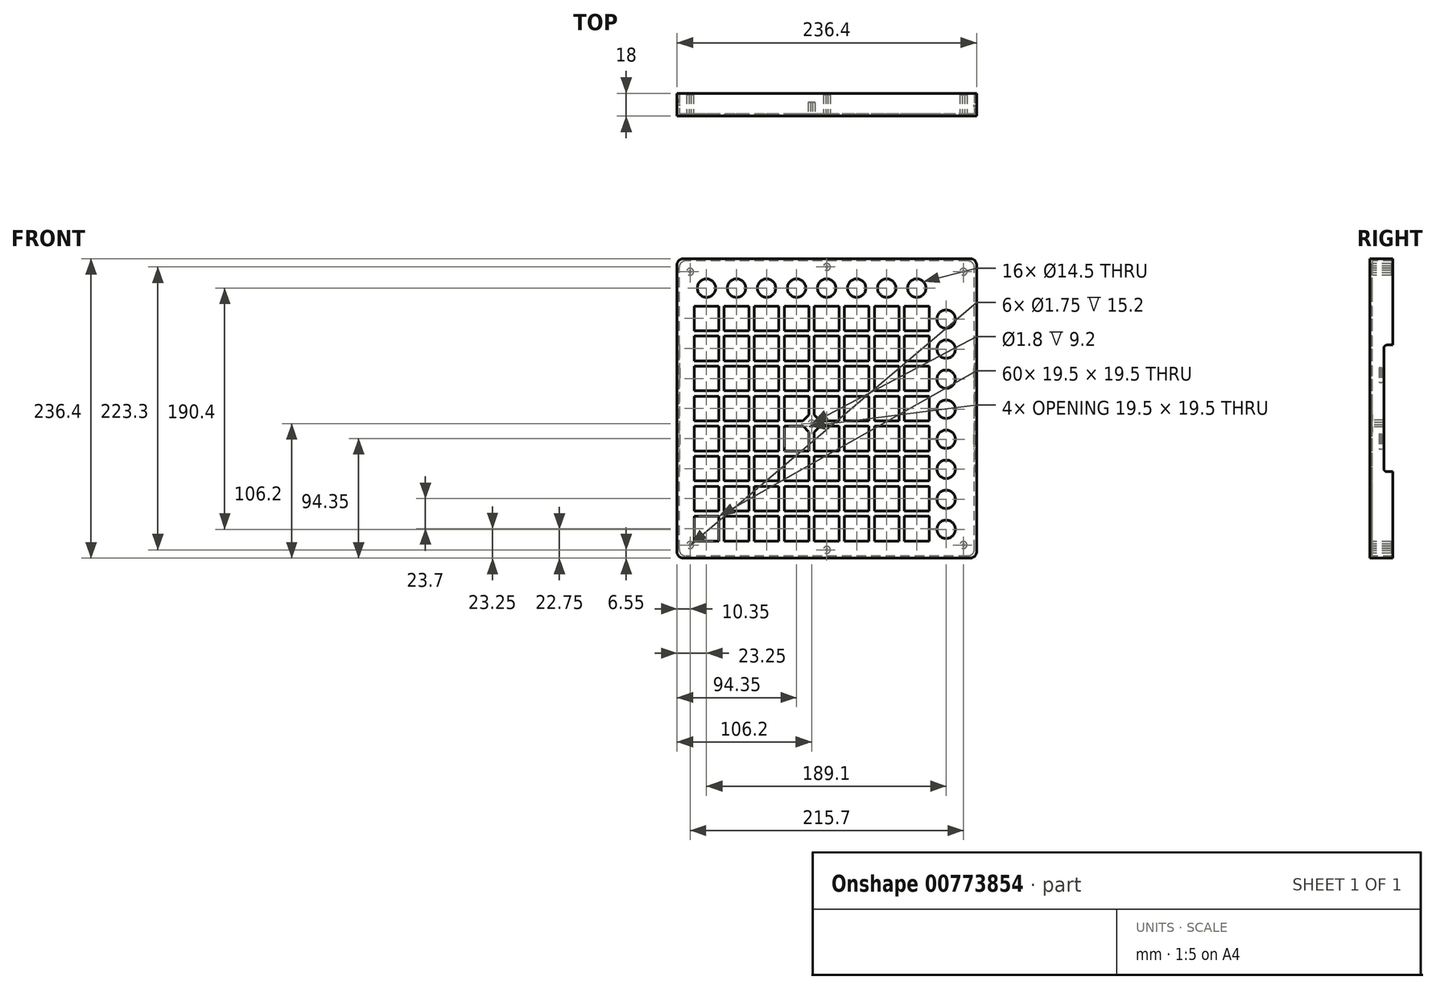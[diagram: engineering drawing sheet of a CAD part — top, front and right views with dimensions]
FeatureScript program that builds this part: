
annotation { "Feature Type Name" : "Feature", "Feature Type Description" : "" }
export const myFeature = defineFeature(function(context is Context, id is Id, definition is map)
    precondition{}
    {
        {
            var Q0;
            Q0=qCreatedBy(makeId("Front.planeOp"),FACE);
            var sketch = newSketch(context, id + "F0", { "sketchPlane" : qUnion([Q0]), "disableImprinting" : false});
            skLineSegment(sketch, "E0.bottom", {"start": v(113.2, -118.2) * mm, "end": v(-113.2, -118.2) * mm});
            skLineSegment(sketch, "E0.top", {"start": v(113.2, 118.2) * mm, "end": v(-113.2, 118.2) * mm});
            skLineSegment(sketch, "E0.left", {"start": v(118.2, -113.2) * mm, "end": v(118.2, 113.2) * mm});
            skLineSegment(sketch, "E0.right", {"start": v(-118.2, -113.2) * mm, "end": v(-118.2, 113.2) * mm});
            skPoint(sketch, "E0.middle", {"position": v(0, 0) * mm});
            skCircle(sketch, "E1", {"center": v(94.15, 70.45) * mm, "radius": 7.25 * mm});
            skCircle(sketch, "E2", {"center": v(94.15, 46.75) * mm, "radius": 7.25 * mm});
            skCircle(sketch, "E3", {"center": v(94.15, 23.05) * mm, "radius": 7.25 * mm});
            skCircle(sketch, "E4", {"center": v(94.15, -0.65) * mm, "radius": 7.25 * mm});
            skCircle(sketch, "E5", {"center": v(94.15, -24.35) * mm, "radius": 7.25 * mm});
            skCircle(sketch, "E6", {"center": v(94.15, -48.05) * mm, "radius": 7.25 * mm});
            skCircle(sketch, "E7", {"center": v(94.15, -71.75) * mm, "radius": 7.25 * mm});
            skCircle(sketch, "E8", {"center": v(94.15, -95.45) * mm, "radius": 7.25 * mm});
            skCircle(sketch, "E9", {"center": v(70.95, 94.95) * mm, "radius": 7.25 * mm});
            skCircle(sketch, "E10", {"center": v(23.55, 94.95) * mm, "radius": 7.25 * mm});
            skCircle(sketch, "E11", {"center": v(47.25, 94.95) * mm, "radius": 7.25 * mm});
            skCircle(sketch, "E12", {"center": v(-0.15, 94.95) * mm, "radius": 7.25 * mm});
            skCircle(sketch, "E13", {"center": v(-23.85, 94.95) * mm, "radius": 7.25 * mm});
            skCircle(sketch, "E14", {"center": v(-47.55, 94.95) * mm, "radius": 7.25 * mm});
            skCircle(sketch, "E15", {"center": v(-71.25, 94.95) * mm, "radius": 7.25 * mm});
            skCircle(sketch, "E16", {"center": v(-94.95, 94.95) * mm, "radius": 7.25 * mm});
            skLineSegment(sketch, "E17.bottom", {"start": v(80.7, 61.2) * mm, "end": v(61.2, 61.2) * mm});
            skLineSegment(sketch, "E17.top", {"start": v(80.7, 80.7) * mm, "end": v(61.2, 80.7) * mm});
            skLineSegment(sketch, "E17.left", {"start": v(80.7, 61.2) * mm, "end": v(80.7, 80.7) * mm});
            skLineSegment(sketch, "E17.right", {"start": v(61.2, 61.2) * mm, "end": v(61.2, 80.7) * mm});
            skPoint(sketch, "E17.middle", {"position": v(70.95, 70.95) * mm});
            skLineSegment(sketch, "E18.bottom", {"start": v(80.7, 37.5) * mm, "end": v(61.2, 37.5) * mm});
            skLineSegment(sketch, "E18.top", {"start": v(80.7, 57) * mm, "end": v(61.2, 57) * mm});
            skLineSegment(sketch, "E18.left", {"start": v(80.7, 37.5) * mm, "end": v(80.7, 57) * mm});
            skLineSegment(sketch, "E18.right", {"start": v(61.2, 37.5) * mm, "end": v(61.2, 57) * mm});
            skLineSegment(sketch, "E19.bottom", {"start": v(80.7, 13.8) * mm, "end": v(61.2, 13.8) * mm});
            skLineSegment(sketch, "E19.top", {"start": v(80.7, 33.3) * mm, "end": v(61.2, 33.3) * mm});
            skLineSegment(sketch, "E19.left", {"start": v(80.7, 13.8) * mm, "end": v(80.7, 33.3) * mm});
            skLineSegment(sketch, "E19.right", {"start": v(61.2, 13.8) * mm, "end": v(61.2, 33.3) * mm});
            skLineSegment(sketch, "E20.bottom", {"start": v(80.7, -9.9) * mm, "end": v(61.2, -9.9) * mm});
            skLineSegment(sketch, "E20.top", {"start": v(80.7, 9.6) * mm, "end": v(61.2, 9.6) * mm});
            skLineSegment(sketch, "E20.left", {"start": v(80.7, -9.9) * mm, "end": v(80.7, 9.6) * mm});
            skLineSegment(sketch, "E20.right", {"start": v(61.2, -9.9) * mm, "end": v(61.2, 9.6) * mm});
            skLineSegment(sketch, "E21.bottom", {"start": v(80.7, -33.6) * mm, "end": v(61.2, -33.6) * mm});
            skLineSegment(sketch, "E21.top", {"start": v(80.7, -14.1) * mm, "end": v(61.2, -14.1) * mm});
            skLineSegment(sketch, "E21.left", {"start": v(80.7, -33.6) * mm, "end": v(80.7, -14.1) * mm});
            skLineSegment(sketch, "E21.right", {"start": v(61.2, -33.6) * mm, "end": v(61.2, -14.1) * mm});
            skLineSegment(sketch, "E22.bottom", {"start": v(80.7, -57.3) * mm, "end": v(61.2, -57.3) * mm});
            skLineSegment(sketch, "E22.top", {"start": v(80.7, -37.8) * mm, "end": v(61.2, -37.8) * mm});
            skLineSegment(sketch, "E22.left", {"start": v(80.7, -57.3) * mm, "end": v(80.7, -37.8) * mm});
            skLineSegment(sketch, "E22.right", {"start": v(61.2, -57.3) * mm, "end": v(61.2, -37.8) * mm});
            skLineSegment(sketch, "E23.bottom", {"start": v(80.7, -81) * mm, "end": v(61.2, -81) * mm});
            skLineSegment(sketch, "E23.top", {"start": v(80.7, -61.5) * mm, "end": v(61.2, -61.5) * mm});
            skLineSegment(sketch, "E23.left", {"start": v(80.7, -81) * mm, "end": v(80.7, -61.5) * mm});
            skLineSegment(sketch, "E23.right", {"start": v(61.2, -81) * mm, "end": v(61.2, -61.5) * mm});
            skLineSegment(sketch, "E24.bottom", {"start": v(80.7, -104.7) * mm, "end": v(61.2, -104.7) * mm});
            skLineSegment(sketch, "E24.top", {"start": v(80.7, -85.2) * mm, "end": v(61.2, -85.2) * mm});
            skLineSegment(sketch, "E24.left", {"start": v(80.7, -104.7) * mm, "end": v(80.7, -85.2) * mm});
            skLineSegment(sketch, "E24.right", {"start": v(61.2, -104.7) * mm, "end": v(61.2, -85.2) * mm});
            skLineSegment(sketch, "E25.bottom", {"start": v(57, 61.2) * mm, "end": v(37.5, 61.2) * mm});
            skLineSegment(sketch, "E25.top", {"start": v(57, 80.7) * mm, "end": v(37.5, 80.7) * mm});
            skLineSegment(sketch, "E25.left", {"start": v(57, 61.2) * mm, "end": v(57, 80.7) * mm});
            skLineSegment(sketch, "E25.right", {"start": v(37.5, 61.2) * mm, "end": v(37.5, 80.7) * mm});
            skLineSegment(sketch, "E26.bottom", {"start": v(57, 37.5) * mm, "end": v(37.5, 37.5) * mm});
            skLineSegment(sketch, "E26.top", {"start": v(57, 57) * mm, "end": v(37.5, 57) * mm});
            skLineSegment(sketch, "E26.left", {"start": v(57, 37.5) * mm, "end": v(57, 57) * mm});
            skLineSegment(sketch, "E26.right", {"start": v(37.5, 37.5) * mm, "end": v(37.5, 57) * mm});
            skLineSegment(sketch, "E27.bottom", {"start": v(57, 13.8) * mm, "end": v(37.5, 13.8) * mm});
            skLineSegment(sketch, "E27.top", {"start": v(57, 33.3) * mm, "end": v(37.5, 33.3) * mm});
            skLineSegment(sketch, "E27.left", {"start": v(57, 13.8) * mm, "end": v(57, 33.3) * mm});
            skLineSegment(sketch, "E27.right", {"start": v(37.5, 13.8) * mm, "end": v(37.5, 33.3) * mm});
            skLineSegment(sketch, "E28.bottom", {"start": v(57, -9.9) * mm, "end": v(37.5, -9.9) * mm});
            skLineSegment(sketch, "E28.top", {"start": v(57, 9.6) * mm, "end": v(37.5, 9.6) * mm});
            skLineSegment(sketch, "E28.left", {"start": v(57, -9.9) * mm, "end": v(57, 9.6) * mm});
            skLineSegment(sketch, "E28.right", {"start": v(37.5, -9.9) * mm, "end": v(37.5, 9.6) * mm});
            skLineSegment(sketch, "E29.bottom", {"start": v(57, -33.6) * mm, "end": v(37.5, -33.6) * mm});
            skLineSegment(sketch, "E29.top", {"start": v(57, -14.1) * mm, "end": v(37.5, -14.1) * mm});
            skLineSegment(sketch, "E29.left", {"start": v(57, -33.6) * mm, "end": v(57, -14.1) * mm});
            skLineSegment(sketch, "E29.right", {"start": v(37.5, -33.6) * mm, "end": v(37.5, -14.1) * mm});
            skLineSegment(sketch, "E30.bottom", {"start": v(57, -57.3) * mm, "end": v(37.5, -57.3) * mm});
            skLineSegment(sketch, "E30.top", {"start": v(57, -37.8) * mm, "end": v(37.5, -37.8) * mm});
            skLineSegment(sketch, "E30.left", {"start": v(57, -57.3) * mm, "end": v(57, -37.8) * mm});
            skLineSegment(sketch, "E30.right", {"start": v(37.5, -57.3) * mm, "end": v(37.5, -37.8) * mm});
            skLineSegment(sketch, "E31.bottom", {"start": v(57, -81) * mm, "end": v(37.5, -81) * mm});
            skLineSegment(sketch, "E31.top", {"start": v(57, -61.5) * mm, "end": v(37.5, -61.5) * mm});
            skLineSegment(sketch, "E31.left", {"start": v(57, -81) * mm, "end": v(57, -61.5) * mm});
            skLineSegment(sketch, "E31.right", {"start": v(37.5, -81) * mm, "end": v(37.5, -61.5) * mm});
            skLineSegment(sketch, "E32.bottom", {"start": v(57, -104.7) * mm, "end": v(37.5, -104.7) * mm});
            skLineSegment(sketch, "E32.top", {"start": v(57, -85.2) * mm, "end": v(37.5, -85.2) * mm});
            skLineSegment(sketch, "E32.left", {"start": v(57, -104.7) * mm, "end": v(57, -85.2) * mm});
            skLineSegment(sketch, "E33", {"start": v(37.5, -85.2) * mm, "end": v(37.5, -104.7) * mm});
            skLineSegment(sketch, "E34.bottom", {"start": v(33.3, 61.2) * mm, "end": v(13.8, 61.2) * mm});
            skLineSegment(sketch, "E34.top", {"start": v(33.3, 80.7) * mm, "end": v(13.8, 80.7) * mm});
            skLineSegment(sketch, "E34.left", {"start": v(33.3, 61.2) * mm, "end": v(33.3, 80.7) * mm});
            skLineSegment(sketch, "E34.right", {"start": v(13.8, 61.2) * mm, "end": v(13.8, 80.7) * mm});
            skLineSegment(sketch, "E35.bottom", {"start": v(33.3, 37.5) * mm, "end": v(13.8, 37.5) * mm});
            skLineSegment(sketch, "E35.top", {"start": v(33.3, 57) * mm, "end": v(13.8, 57) * mm});
            skLineSegment(sketch, "E35.left", {"start": v(33.3, 37.5) * mm, "end": v(33.3, 57) * mm});
            skLineSegment(sketch, "E35.right", {"start": v(13.8, 37.5) * mm, "end": v(13.8, 57) * mm});
            skLineSegment(sketch, "E36.bottom", {"start": v(33.3, 13.8) * mm, "end": v(13.8, 13.8) * mm});
            skLineSegment(sketch, "E36.top", {"start": v(33.3, 33.3) * mm, "end": v(13.8, 33.3) * mm});
            skLineSegment(sketch, "E36.left", {"start": v(33.3, 13.8) * mm, "end": v(33.3, 33.3) * mm});
            skLineSegment(sketch, "E36.right", {"start": v(13.8, 13.8) * mm, "end": v(13.8, 33.3) * mm});
            skLineSegment(sketch, "E37.bottom", {"start": v(33.3, -9.9) * mm, "end": v(13.8, -9.9) * mm});
            skLineSegment(sketch, "E37.top", {"start": v(33.3, 9.6) * mm, "end": v(13.8, 9.6) * mm});
            skLineSegment(sketch, "E37.left", {"start": v(33.3, -9.9) * mm, "end": v(33.3, 9.6) * mm});
            skLineSegment(sketch, "E37.right", {"start": v(13.8, -9.9) * mm, "end": v(13.8, 9.6) * mm});
            skLineSegment(sketch, "E38.bottom", {"start": v(33.3, -33.6) * mm, "end": v(13.8, -33.6) * mm});
            skLineSegment(sketch, "E38.top", {"start": v(33.3, -14.1) * mm, "end": v(13.8, -14.1) * mm});
            skLineSegment(sketch, "E38.left", {"start": v(33.3, -33.6) * mm, "end": v(33.3, -14.1) * mm});
            skLineSegment(sketch, "E38.right", {"start": v(13.8, -33.6) * mm, "end": v(13.8, -14.1) * mm});
            skLineSegment(sketch, "E39.bottom", {"start": v(33.3, -57.3) * mm, "end": v(13.8, -57.3) * mm});
            skLineSegment(sketch, "E39.top", {"start": v(33.3, -37.8) * mm, "end": v(13.8, -37.8) * mm});
            skLineSegment(sketch, "E39.left", {"start": v(33.3, -57.3) * mm, "end": v(33.3, -37.8) * mm});
            skLineSegment(sketch, "E39.right", {"start": v(13.8, -57.3) * mm, "end": v(13.8, -37.8) * mm});
            skLineSegment(sketch, "E40.bottom", {"start": v(33.3, -81) * mm, "end": v(13.8, -81) * mm});
            skLineSegment(sketch, "E40.top", {"start": v(33.3, -61.5) * mm, "end": v(13.8, -61.5) * mm});
            skLineSegment(sketch, "E40.left", {"start": v(33.3, -81) * mm, "end": v(33.3, -61.5) * mm});
            skLineSegment(sketch, "E40.right", {"start": v(13.8, -81) * mm, "end": v(13.8, -61.5) * mm});
            skLineSegment(sketch, "E41.bottom", {"start": v(33.3, -104.7) * mm, "end": v(13.8, -104.7) * mm});
            skLineSegment(sketch, "E41.top", {"start": v(33.3, -85.2) * mm, "end": v(13.8, -85.2) * mm});
            skLineSegment(sketch, "E41.left", {"start": v(33.3, -104.7) * mm, "end": v(33.3, -85.2) * mm});
            skLineSegment(sketch, "E42.bottom", {"start": v(9.6, 61.2) * mm, "end": v(-9.9, 61.2) * mm});
            skLineSegment(sketch, "E42.top", {"start": v(9.6, 80.7) * mm, "end": v(-9.9, 80.7) * mm});
            skLineSegment(sketch, "E42.left", {"start": v(9.6, 61.2) * mm, "end": v(9.6, 80.7) * mm});
            skLineSegment(sketch, "E42.right", {"start": v(-9.9, 61.2) * mm, "end": v(-9.9, 80.7) * mm});
            skLineSegment(sketch, "E43.bottom", {"start": v(9.6, 37.5) * mm, "end": v(-9.9, 37.5) * mm});
            skLineSegment(sketch, "E43.top", {"start": v(9.6, 57) * mm, "end": v(-9.9, 57) * mm});
            skLineSegment(sketch, "E43.left", {"start": v(9.6, 37.5) * mm, "end": v(9.6, 57) * mm});
            skLineSegment(sketch, "E43.right", {"start": v(-9.9, 37.5) * mm, "end": v(-9.9, 57) * mm});
            skLineSegment(sketch, "E44.bottom", {"start": v(9.6, 13.8) * mm, "end": v(-9.9, 13.8) * mm});
            skLineSegment(sketch, "E44.top", {"start": v(9.6, 33.3) * mm, "end": v(-9.9, 33.3) * mm});
            skLineSegment(sketch, "E44.left", {"start": v(9.6, 13.8) * mm, "end": v(9.6, 33.3) * mm});
            skLineSegment(sketch, "E44.right", {"start": v(-9.9, 13.8) * mm, "end": v(-9.9, 33.3) * mm});
            skLineSegment(sketch, "E45.bottom", {"start": v(9.6, -9.9) * mm, "end": v(-9.9, -9.9) * mm});
            skLineSegment(sketch, "E45.top", {"start": v(9.6, 9.6) * mm, "end": v(-9.9, 9.6) * mm});
            skLineSegment(sketch, "E45.left", {"start": v(9.6, -9.9) * mm, "end": v(9.6, 9.6) * mm});
            skLineSegment(sketch, "E45.right", {"start": v(-9.9, -9.9) * mm, "end": v(-9.9, 9.6) * mm});
            skLineSegment(sketch, "E46.bottom", {"start": v(9.6, -33.6) * mm, "end": v(-9.9, -33.6) * mm});
            skLineSegment(sketch, "E46.top", {"start": v(9.6, -14.1) * mm, "end": v(-9.9, -14.1) * mm});
            skLineSegment(sketch, "E46.left", {"start": v(9.6, -33.6) * mm, "end": v(9.6, -14.1) * mm});
            skLineSegment(sketch, "E46.right", {"start": v(-9.9, -33.6) * mm, "end": v(-9.9, -14.1) * mm});
            skLineSegment(sketch, "E47.bottom", {"start": v(9.6, -57.3) * mm, "end": v(-9.9, -57.3) * mm});
            skLineSegment(sketch, "E47.top", {"start": v(9.6, -37.8) * mm, "end": v(-9.9, -37.8) * mm});
            skLineSegment(sketch, "E47.left", {"start": v(9.6, -57.3) * mm, "end": v(9.6, -37.8) * mm});
            skLineSegment(sketch, "E47.right", {"start": v(-9.9, -57.3) * mm, "end": v(-9.9, -37.8) * mm});
            skLineSegment(sketch, "E48.bottom", {"start": v(9.6, -81) * mm, "end": v(-9.9, -81) * mm});
            skLineSegment(sketch, "E48.top", {"start": v(9.6, -61.5) * mm, "end": v(-9.9, -61.5) * mm});
            skLineSegment(sketch, "E48.left", {"start": v(9.6, -81) * mm, "end": v(9.6, -61.5) * mm});
            skLineSegment(sketch, "E48.right", {"start": v(-9.9, -81) * mm, "end": v(-9.9, -61.5) * mm});
            skLineSegment(sketch, "E49.bottom", {"start": v(9.6, -104.7) * mm, "end": v(-9.9, -104.7) * mm});
            skLineSegment(sketch, "E49.top", {"start": v(9.6, -85.2) * mm, "end": v(-9.9, -85.2) * mm});
            skLineSegment(sketch, "E49.left", {"start": v(9.6, -104.7) * mm, "end": v(9.6, -85.2) * mm});
            skLineSegment(sketch, "E50", {"start": v(13.8, -85.2) * mm, "end": v(13.8, -104.7) * mm});
            skLineSegment(sketch, "E51", {"start": v(-9.9, -85.2) * mm, "end": v(-9.9, -104.7) * mm});
            skLineSegment(sketch, "E52.bottom", {"start": v(-14.1, 61.2) * mm, "end": v(-33.6, 61.2) * mm});
            skLineSegment(sketch, "E52.top", {"start": v(-14.1, 80.7) * mm, "end": v(-33.6, 80.7) * mm});
            skLineSegment(sketch, "E52.left", {"start": v(-14.1, 61.2) * mm, "end": v(-14.1, 80.7) * mm});
            skLineSegment(sketch, "E52.right", {"start": v(-33.6, 61.2) * mm, "end": v(-33.6, 80.7) * mm});
            skLineSegment(sketch, "E53.bottom", {"start": v(-14.1, 37.5) * mm, "end": v(-33.6, 37.5) * mm});
            skLineSegment(sketch, "E53.top", {"start": v(-14.1, 57) * mm, "end": v(-33.6, 57) * mm});
            skLineSegment(sketch, "E53.left", {"start": v(-14.1, 37.5) * mm, "end": v(-14.1, 57) * mm});
            skLineSegment(sketch, "E53.right", {"start": v(-33.6, 37.5) * mm, "end": v(-33.6, 57) * mm});
            skLineSegment(sketch, "E54.bottom", {"start": v(-14.1, 13.8) * mm, "end": v(-33.6, 13.8) * mm});
            skLineSegment(sketch, "E54.top", {"start": v(-14.1, 33.3) * mm, "end": v(-33.6, 33.3) * mm});
            skLineSegment(sketch, "E54.left", {"start": v(-14.1, 13.8) * mm, "end": v(-14.1, 33.3) * mm});
            skLineSegment(sketch, "E54.right", {"start": v(-33.6, 13.8) * mm, "end": v(-33.6, 33.3) * mm});
            skLineSegment(sketch, "E55.bottom", {"start": v(-14.1, -9.9) * mm, "end": v(-33.6, -9.9) * mm});
            skLineSegment(sketch, "E55.top", {"start": v(-14.1, 9.6) * mm, "end": v(-33.6, 9.6) * mm});
            skLineSegment(sketch, "E55.left", {"start": v(-14.1, -9.9) * mm, "end": v(-14.1, 9.6) * mm});
            skLineSegment(sketch, "E55.right", {"start": v(-33.6, -9.9) * mm, "end": v(-33.6, 9.6) * mm});
            skLineSegment(sketch, "E56.bottom", {"start": v(-14.1, -33.6) * mm, "end": v(-33.6, -33.6) * mm});
            skLineSegment(sketch, "E56.top", {"start": v(-14.1, -14.1) * mm, "end": v(-33.6, -14.1) * mm});
            skLineSegment(sketch, "E56.left", {"start": v(-14.1, -33.6) * mm, "end": v(-14.1, -14.1) * mm});
            skLineSegment(sketch, "E56.right", {"start": v(-33.6, -33.6) * mm, "end": v(-33.6, -14.1) * mm});
            skLineSegment(sketch, "E57.bottom", {"start": v(-14.1, -57.3) * mm, "end": v(-33.6, -57.3) * mm});
            skLineSegment(sketch, "E57.top", {"start": v(-14.1, -37.8) * mm, "end": v(-33.6, -37.8) * mm});
            skLineSegment(sketch, "E57.left", {"start": v(-14.1, -57.3) * mm, "end": v(-14.1, -37.8) * mm});
            skLineSegment(sketch, "E57.right", {"start": v(-33.6, -57.3) * mm, "end": v(-33.6, -37.8) * mm});
            skLineSegment(sketch, "E58.bottom", {"start": v(-14.1, -81) * mm, "end": v(-33.6, -81) * mm});
            skLineSegment(sketch, "E58.top", {"start": v(-14.1, -61.5) * mm, "end": v(-33.6, -61.5) * mm});
            skLineSegment(sketch, "E58.left", {"start": v(-14.1, -81) * mm, "end": v(-14.1, -61.5) * mm});
            skLineSegment(sketch, "E58.right", {"start": v(-33.6, -81) * mm, "end": v(-33.6, -61.5) * mm});
            skLineSegment(sketch, "E59.bottom", {"start": v(-14.1, -104.7) * mm, "end": v(-33.6, -104.7) * mm});
            skLineSegment(sketch, "E59.top", {"start": v(-14.1, -85.2) * mm, "end": v(-33.6, -85.2) * mm});
            skLineSegment(sketch, "E59.left", {"start": v(-14.1, -104.7) * mm, "end": v(-14.1, -85.2) * mm});
            skLineSegment(sketch, "E60", {"start": v(-33.6, -85.2) * mm, "end": v(-33.6, -104.7) * mm});
            skLineSegment(sketch, "E61.bottom", {"start": v(-37.8, 61.2) * mm, "end": v(-57.3, 61.2) * mm});
            skLineSegment(sketch, "E61.top", {"start": v(-37.8, 80.7) * mm, "end": v(-57.3, 80.7) * mm});
            skLineSegment(sketch, "E61.left", {"start": v(-37.8, 61.2) * mm, "end": v(-37.8, 80.7) * mm});
            skLineSegment(sketch, "E61.right", {"start": v(-57.3, 61.2) * mm, "end": v(-57.3, 80.7) * mm});
            skLineSegment(sketch, "E62.bottom", {"start": v(-37.8, 37.5) * mm, "end": v(-57.3, 37.5) * mm});
            skLineSegment(sketch, "E62.top", {"start": v(-37.8, 57) * mm, "end": v(-57.3, 57) * mm});
            skLineSegment(sketch, "E62.left", {"start": v(-37.8, 37.5) * mm, "end": v(-37.8, 57) * mm});
            skLineSegment(sketch, "E62.right", {"start": v(-57.3, 37.5) * mm, "end": v(-57.3, 57) * mm});
            skLineSegment(sketch, "E63.bottom", {"start": v(-37.8, 13.8) * mm, "end": v(-57.3, 13.8) * mm});
            skLineSegment(sketch, "E63.top", {"start": v(-37.8, 33.3) * mm, "end": v(-57.3, 33.3) * mm});
            skLineSegment(sketch, "E63.left", {"start": v(-37.8, 13.8) * mm, "end": v(-37.8, 33.3) * mm});
            skLineSegment(sketch, "E63.right", {"start": v(-57.3, 13.8) * mm, "end": v(-57.3, 33.3) * mm});
            skLineSegment(sketch, "E64.bottom", {"start": v(-37.8, -9.9) * mm, "end": v(-57.3, -9.9) * mm});
            skLineSegment(sketch, "E64.top", {"start": v(-37.8, 9.6) * mm, "end": v(-57.3, 9.6) * mm});
            skLineSegment(sketch, "E64.left", {"start": v(-37.8, -9.9) * mm, "end": v(-37.8, 9.6) * mm});
            skLineSegment(sketch, "E64.right", {"start": v(-57.3, -9.9) * mm, "end": v(-57.3, 9.6) * mm});
            skLineSegment(sketch, "E65.bottom", {"start": v(-37.8, -33.6) * mm, "end": v(-57.3, -33.6) * mm});
            skLineSegment(sketch, "E65.top", {"start": v(-37.8, -14.1) * mm, "end": v(-57.3, -14.1) * mm});
            skLineSegment(sketch, "E65.left", {"start": v(-37.8, -33.6) * mm, "end": v(-37.8, -14.1) * mm});
            skLineSegment(sketch, "E65.right", {"start": v(-57.3, -33.6) * mm, "end": v(-57.3, -14.1) * mm});
            skLineSegment(sketch, "E66.bottom", {"start": v(-37.8, -57.3) * mm, "end": v(-57.3, -57.3) * mm});
            skLineSegment(sketch, "E66.top", {"start": v(-37.8, -37.8) * mm, "end": v(-57.3, -37.8) * mm});
            skLineSegment(sketch, "E66.left", {"start": v(-37.8, -57.3) * mm, "end": v(-37.8, -37.8) * mm});
            skLineSegment(sketch, "E66.right", {"start": v(-57.3, -57.3) * mm, "end": v(-57.3, -37.8) * mm});
            skLineSegment(sketch, "E67.bottom", {"start": v(-37.8, -81) * mm, "end": v(-57.3, -81) * mm});
            skLineSegment(sketch, "E67.top", {"start": v(-37.8, -61.5) * mm, "end": v(-57.3, -61.5) * mm});
            skLineSegment(sketch, "E67.left", {"start": v(-37.8, -81) * mm, "end": v(-37.8, -61.5) * mm});
            skLineSegment(sketch, "E67.right", {"start": v(-57.3, -81) * mm, "end": v(-57.3, -61.5) * mm});
            skLineSegment(sketch, "E68.bottom", {"start": v(-37.8, -104.7) * mm, "end": v(-57.3, -104.7) * mm});
            skLineSegment(sketch, "E68.top", {"start": v(-37.8, -85.2) * mm, "end": v(-57.3, -85.2) * mm});
            skLineSegment(sketch, "E68.left", {"start": v(-37.8, -104.7) * mm, "end": v(-37.8, -85.2) * mm});
            skLineSegment(sketch, "E69.bottom", {"start": v(-61.5, 61.2) * mm, "end": v(-81, 61.2) * mm});
            skLineSegment(sketch, "E69.top", {"start": v(-61.5, 80.7) * mm, "end": v(-81, 80.7) * mm});
            skLineSegment(sketch, "E69.left", {"start": v(-61.5, 61.2) * mm, "end": v(-61.5, 80.7) * mm});
            skLineSegment(sketch, "E69.right", {"start": v(-81, 61.2) * mm, "end": v(-81, 80.7) * mm});
            skLineSegment(sketch, "E70.bottom", {"start": v(-61.5, 37.5) * mm, "end": v(-81, 37.5) * mm});
            skLineSegment(sketch, "E70.top", {"start": v(-61.5, 57) * mm, "end": v(-81, 57) * mm});
            skLineSegment(sketch, "E70.left", {"start": v(-61.5, 37.5) * mm, "end": v(-61.5, 57) * mm});
            skLineSegment(sketch, "E70.right", {"start": v(-81, 37.5) * mm, "end": v(-81, 57) * mm});
            skLineSegment(sketch, "E71.bottom", {"start": v(-61.5, 13.8) * mm, "end": v(-81, 13.8) * mm});
            skLineSegment(sketch, "E71.top", {"start": v(-61.5, 33.3) * mm, "end": v(-81, 33.3) * mm});
            skLineSegment(sketch, "E71.left", {"start": v(-61.5, 13.8) * mm, "end": v(-61.5, 33.3) * mm});
            skLineSegment(sketch, "E71.right", {"start": v(-81, 13.8) * mm, "end": v(-81, 33.3) * mm});
            skLineSegment(sketch, "E72.bottom", {"start": v(-61.5, -9.9) * mm, "end": v(-81, -9.9) * mm});
            skLineSegment(sketch, "E72.top", {"start": v(-61.5, 9.6) * mm, "end": v(-81, 9.6) * mm});
            skLineSegment(sketch, "E72.left", {"start": v(-61.5, -9.9) * mm, "end": v(-61.5, 9.6) * mm});
            skLineSegment(sketch, "E72.right", {"start": v(-81, -9.9) * mm, "end": v(-81, 9.6) * mm});
            skLineSegment(sketch, "E73.bottom", {"start": v(-61.5, -33.6) * mm, "end": v(-81, -33.6) * mm});
            skLineSegment(sketch, "E73.top", {"start": v(-61.5, -14.1) * mm, "end": v(-81, -14.1) * mm});
            skLineSegment(sketch, "E73.left", {"start": v(-61.5, -33.6) * mm, "end": v(-61.5, -14.1) * mm});
            skLineSegment(sketch, "E73.right", {"start": v(-81, -33.6) * mm, "end": v(-81, -14.1) * mm});
            skLineSegment(sketch, "E74.bottom", {"start": v(-61.5, -57.3) * mm, "end": v(-81, -57.3) * mm});
            skLineSegment(sketch, "E74.top", {"start": v(-61.5, -37.8) * mm, "end": v(-81, -37.8) * mm});
            skLineSegment(sketch, "E74.left", {"start": v(-61.5, -57.3) * mm, "end": v(-61.5, -37.8) * mm});
            skLineSegment(sketch, "E74.right", {"start": v(-81, -57.3) * mm, "end": v(-81, -37.8) * mm});
            skLineSegment(sketch, "E75.bottom", {"start": v(-61.5, -81) * mm, "end": v(-81, -81) * mm});
            skLineSegment(sketch, "E75.top", {"start": v(-61.5, -61.5) * mm, "end": v(-81, -61.5) * mm});
            skLineSegment(sketch, "E75.left", {"start": v(-61.5, -81) * mm, "end": v(-61.5, -61.5) * mm});
            skLineSegment(sketch, "E75.right", {"start": v(-81, -81) * mm, "end": v(-81, -61.5) * mm});
            skLineSegment(sketch, "E76.bottom", {"start": v(-61.5, -104.7) * mm, "end": v(-81, -104.7) * mm});
            skLineSegment(sketch, "E76.top", {"start": v(-61.5, -85.2) * mm, "end": v(-81, -85.2) * mm});
            skLineSegment(sketch, "E76.left", {"start": v(-61.5, -104.7) * mm, "end": v(-61.5, -85.2) * mm});
            skLineSegment(sketch, "E77.bottom", {"start": v(-85.2, 61.2) * mm, "end": v(-104.7, 61.2) * mm});
            skLineSegment(sketch, "E77.top", {"start": v(-85.2, 80.7) * mm, "end": v(-104.7, 80.7) * mm});
            skLineSegment(sketch, "E77.left", {"start": v(-85.2, 61.2) * mm, "end": v(-85.2, 80.7) * mm});
            skLineSegment(sketch, "E77.right", {"start": v(-104.7, 61.2) * mm, "end": v(-104.7, 80.7) * mm});
            skLineSegment(sketch, "E78.bottom", {"start": v(-85.2, 37.5) * mm, "end": v(-104.7, 37.5) * mm});
            skLineSegment(sketch, "E78.top", {"start": v(-85.2, 57) * mm, "end": v(-104.7, 57) * mm});
            skLineSegment(sketch, "E78.left", {"start": v(-85.2, 37.5) * mm, "end": v(-85.2, 57) * mm});
            skLineSegment(sketch, "E78.right", {"start": v(-104.7, 37.5) * mm, "end": v(-104.7, 57) * mm});
            skLineSegment(sketch, "E79.bottom", {"start": v(-85.2, 13.8) * mm, "end": v(-104.7, 13.8) * mm});
            skLineSegment(sketch, "E79.top", {"start": v(-85.2, 33.3) * mm, "end": v(-104.7, 33.3) * mm});
            skLineSegment(sketch, "E79.left", {"start": v(-85.2, 13.8) * mm, "end": v(-85.2, 33.3) * mm});
            skLineSegment(sketch, "E79.right", {"start": v(-104.7, 13.8) * mm, "end": v(-104.7, 33.3) * mm});
            skLineSegment(sketch, "E80.bottom", {"start": v(-85.2, -9.9) * mm, "end": v(-104.7, -9.9) * mm});
            skLineSegment(sketch, "E80.top", {"start": v(-85.2, 9.6) * mm, "end": v(-104.7, 9.6) * mm});
            skLineSegment(sketch, "E80.left", {"start": v(-85.2, -9.9) * mm, "end": v(-85.2, 9.6) * mm});
            skLineSegment(sketch, "E80.right", {"start": v(-104.7, -9.9) * mm, "end": v(-104.7, 9.6) * mm});
            skLineSegment(sketch, "E81.bottom", {"start": v(-85.2, -33.6) * mm, "end": v(-104.7, -33.6) * mm});
            skLineSegment(sketch, "E81.top", {"start": v(-85.2, -14.1) * mm, "end": v(-104.7, -14.1) * mm});
            skLineSegment(sketch, "E81.left", {"start": v(-85.2, -33.6) * mm, "end": v(-85.2, -14.1) * mm});
            skLineSegment(sketch, "E81.right", {"start": v(-104.7, -33.6) * mm, "end": v(-104.7, -14.1) * mm});
            skLineSegment(sketch, "E82.bottom", {"start": v(-85.2, -57.3) * mm, "end": v(-104.7, -57.3) * mm});
            skLineSegment(sketch, "E82.top", {"start": v(-85.2, -37.8) * mm, "end": v(-104.7, -37.8) * mm});
            skLineSegment(sketch, "E82.left", {"start": v(-85.2, -57.3) * mm, "end": v(-85.2, -37.8) * mm});
            skLineSegment(sketch, "E82.right", {"start": v(-104.7, -57.3) * mm, "end": v(-104.7, -37.8) * mm});
            skLineSegment(sketch, "E83.bottom", {"start": v(-85.2, -81) * mm, "end": v(-104.7, -81) * mm});
            skLineSegment(sketch, "E83.top", {"start": v(-85.2, -61.5) * mm, "end": v(-104.7, -61.5) * mm});
            skLineSegment(sketch, "E83.left", {"start": v(-85.2, -81) * mm, "end": v(-85.2, -61.5) * mm});
            skLineSegment(sketch, "E83.right", {"start": v(-104.7, -81) * mm, "end": v(-104.7, -61.5) * mm});
            skLineSegment(sketch, "E84.bottom", {"start": v(-85.2, -104.7) * mm, "end": v(-104.7, -104.7) * mm});
            skLineSegment(sketch, "E84.top", {"start": v(-85.2, -85.2) * mm, "end": v(-104.7, -85.2) * mm});
            skLineSegment(sketch, "E84.left", {"start": v(-85.2, -104.7) * mm, "end": v(-85.2, -85.2) * mm});
            skLineSegment(sketch, "E85", {"start": v(-81, -85.2) * mm, "end": v(-81, -104.7) * mm});
            skLineSegment(sketch, "E86", {"start": v(-104.7, -85.2) * mm, "end": v(-104.7, -104.7) * mm});
            skLineSegment(sketch, "E87.bottom", {"start": v(111.4, -116.4) * mm, "end": v(-111.4, -116.4) * mm});
            skLineSegment(sketch, "E87.top", {"start": v(111.4, 116.4) * mm, "end": v(-111.4, 116.4) * mm});
            skLineSegment(sketch, "E87.left", {"start": v(116.4, -111.4) * mm, "end": v(116.4, 111.4) * mm});
            skLineSegment(sketch, "E87.right", {"start": v(-116.4, -111.4) * mm, "end": v(-116.4, 111.4) * mm});
            skLineSegment(sketch, "E88", {"start": v(-57.3, -104.7) * mm, "end": v(-57.3, -85.2) * mm});
            skLineSegment(sketch, "E89.bottom", {"start": v(-3.12, -11.96) * mm, "end": v(-11.96, -20.8) * mm});
            skLineSegment(sketch, "E89.top", {"start": v(-11.96, -3.12) * mm, "end": v(-20.8, -11.96) * mm});
            skLineSegment(sketch, "E89.left", {"start": v(-3.12, -11.96) * mm, "end": v(-11.96, -3.12) * mm});
            skLineSegment(sketch, "E89.right", {"start": v(-11.96, -20.8) * mm, "end": v(-20.8, -11.96) * mm});
            skCircle(sketch, "E90", {"center": v(-12, -12) * mm, "radius": 2.75 * mm});
            skCircle(sketch, "E91", {"center": v(-12, -12) * mm, "radius": 0.9 * mm});
            skCircle(sketch, "E92", {"center": v(0, 111.65) * mm, "radius": 2.75 * mm});
            skCircle(sketch, "E93", {"center": v(0, 111.65) * mm, "radius": 0.88 * mm});
            skCircle(sketch, "E94", {"center": v(0, -111.65) * mm, "radius": 2.75 * mm});
            skCircle(sketch, "E95", {"center": v(0, -111.65) * mm, "radius": 0.88 * mm});
            skCircle(sketch, "E96", {"center": v(107.85, -107.85) * mm, "radius": 2.75 * mm});
            skCircle(sketch, "E97", {"center": v(107.85, -107.85) * mm, "radius": 0.88 * mm});
            skCircle(sketch, "E98", {"center": v(107.85, 107.85) * mm, "radius": 2.75 * mm});
            skCircle(sketch, "E99", {"center": v(107.85, 107.85) * mm, "radius": 0.88 * mm});
            skCircle(sketch, "E100", {"center": v(-107.85, 107.85) * mm, "radius": 2.75 * mm});
            skCircle(sketch, "E101", {"center": v(-107.85, 107.85) * mm, "radius": 0.88 * mm});
            skCircle(sketch, "E102", {"center": v(-107.85, -107.85) * mm, "radius": 2.75 * mm});
            skCircle(sketch, "E103", {"center": v(-107.85, -107.85) * mm, "radius": 0.88 * mm});
            skPoint(sketch, "E104.visualSharp", {"position": v(116.4, 116.4) * mm});
            skArc(sketch, "E104.filletArc", {"start": v(116.4, 111.4) * mm, "mid": v(114.94, 114.94) * mm, "end": v(111.4, 116.4) * mm});
            skPoint(sketch, "E105.visualSharp", {"position": v(118.2, 118.2) * mm});
            skArc(sketch, "E105.filletArc", {"start": v(118.2, 113.2) * mm, "mid": v(116.74, 116.74) * mm, "end": v(113.2, 118.2) * mm});
            skPoint(sketch, "E106.visualSharp", {"position": v(-118.2, 118.2) * mm});
            skArc(sketch, "E106.filletArc", {"start": v(-113.2, 118.2) * mm, "mid": v(-116.74, 116.74) * mm, "end": v(-118.2, 113.2) * mm});
            skPoint(sketch, "E107.visualSharp", {"position": v(-116.4, 116.4) * mm});
            skArc(sketch, "E107.filletArc", {"start": v(-111.4, 116.4) * mm, "mid": v(-114.94, 114.94) * mm, "end": v(-116.4, 111.4) * mm});
            skPoint(sketch, "E108.visualSharp", {"position": v(-116.4, -116.4) * mm});
            skArc(sketch, "E108.filletArc", {"start": v(-116.4, -111.4) * mm, "mid": v(-114.94, -114.94) * mm, "end": v(-111.4, -116.4) * mm});
            skPoint(sketch, "E109.visualSharp", {"position": v(-118.2, -118.2) * mm});
            skArc(sketch, "E109.filletArc", {"start": v(-118.2, -113.2) * mm, "mid": v(-116.74, -116.74) * mm, "end": v(-113.2, -118.2) * mm});
            skPoint(sketch, "E110.visualSharp", {"position": v(116.4, -116.4) * mm});
            skArc(sketch, "E110.filletArc", {"start": v(111.4, -116.4) * mm, "mid": v(114.94, -114.94) * mm, "end": v(116.4, -111.4) * mm});
            skPoint(sketch, "E111.visualSharp", {"position": v(118.2, -118.2) * mm});
            skArc(sketch, "E111.filletArc", {"start": v(113.2, -118.2) * mm, "mid": v(116.74, -116.74) * mm, "end": v(118.2, -113.2) * mm});
            skSolve(sketch);
        }
        {
            var Q0;
            Q0=makeQuery(id+"F0.imprint","IMPRINT",FACE,{"disambiguationData":[TD([[makeQuery(id+"F0.imprint","IMPRINT",EDGE,{"derivedFrom":sQuery(id+"F0.wireOp",EDGE,"E0.bottom")}),-1.0]])]});
            extrude(context, id + "F1", {"entities" : qUnion([Q0]), "depth" : -18 * mm, "offsetDistance" : 25 * mm});
        }
        {
            var Q0;
            Q0=makeQuery(id+"F0.imprint","IMPRINT",FACE,{"disambiguationData":[TD([[makeQuery(id+"F0.imprint","IMPRINT",EDGE,{"derivedFrom":sQuery(id+"F0.wireOp",EDGE,"E1")}),-1.0]])]});
            var Q1;
            {var subQ0=sQuery(id+"F0.wireOp",EDGE,"E55.left");var subQ1=sQuery(id+"F0.wireOp",EDGE,"E55.bottom");var subQ2=makeQuery(id+"F0.imprint","INTERSECT",VERTEX,{"derivedFrom":[subQ1,subQ0]});Q1=makeQuery(id+"F0.imprint","IMPRINT",FACE,{"disambiguationData":[TD([[makeQuery(id+"F0.imprint","IMPRINT",EDGE,{"disambiguationData":[TD([[subQ2,-1.0]])],"derivedFrom":subQ1}),-1.0]])]});}
            var Q2;
            {var subQ9=sQuery(id+"F0.wireOp",EDGE,"E45.right");var subQ10=sQuery(id+"F0.wireOp",EDGE,"E45.bottom");var subQ11=makeQuery(id+"F0.imprint","INTERSECT",VERTEX,{"derivedFrom":[subQ10,subQ9]});Q2=makeQuery(id+"F0.imprint","IMPRINT",FACE,{"disambiguationData":[TD([[makeQuery(id+"F0.imprint","IMPRINT",EDGE,{"disambiguationData":[TD([[subQ11,1.0]])],"derivedFrom":subQ10}),1.0]])]});}
            var Q3;
            {var subQ0=sQuery(id+"F0.wireOp",EDGE,"E56.left");var subQ1=sQuery(id+"F0.wireOp",EDGE,"E56.top");var subQ2=makeQuery(id+"F0.imprint","INTERSECT",VERTEX,{"derivedFrom":[subQ1,subQ0]});Q3=makeQuery(id+"F0.imprint","IMPRINT",FACE,{"disambiguationData":[TD([[makeQuery(id+"F0.imprint","IMPRINT",EDGE,{"disambiguationData":[TD([[subQ2,-1.0]])],"derivedFrom":subQ1}),1.0]])]});}
            var Q4;
            {var subQ0=sQuery(id+"F0.wireOp",EDGE,"E46.right");var subQ1=sQuery(id+"F0.wireOp",EDGE,"E46.top");var subQ2=makeQuery(id+"F0.imprint","INTERSECT",VERTEX,{"derivedFrom":[subQ1,subQ0]});Q4=makeQuery(id+"F0.imprint","IMPRINT",FACE,{"disambiguationData":[TD([[makeQuery(id+"F0.imprint","IMPRINT",EDGE,{"disambiguationData":[TD([[subQ2,1.0]])],"derivedFrom":subQ1}),1.0]])]});}
            var Q5;
            {var subQ0=sQuery(id+"F0.wireOp",EDGE,"E45.right");var subQ1=sQuery(id+"F0.wireOp",EDGE,"E45.bottom");var subQ2=makeQuery(id+"F0.imprint","INTERSECT",VERTEX,{"derivedFrom":[subQ1,subQ0]});Q5=makeQuery(id+"F0.imprint","IMPRINT",FACE,{"disambiguationData":[TD([[makeQuery(id+"F0.imprint","IMPRINT",EDGE,{"disambiguationData":[TD([[subQ2,1.0]])],"derivedFrom":subQ1}),-1.0]])]});}
            extrude(context, id + "F2", {"entities" : qUnion([Q0, Q1, Q2, Q3, Q4, Q5]), "operationType" : NewBodyOperationType.ADD, "depth" : -1.8 * mm, "offsetDistance" : 25 * mm});
        }
        {
            var Q0;
            Q0=makeQuery(id+"F0.imprint","IMPRINT",FACE,{"disambiguationData":[TD([[makeQuery(id+"F0.imprint","IMPRINT",EDGE,{"derivedFrom":sQuery(id+"F0.wireOp",EDGE,"E90")}),1.0]])]});
            extrude(context, id + "F3", {"entities" : qUnion([Q0]), "operationType" : NewBodyOperationType.ADD, "depth" : -17 * mm, "offsetDistance" : 25 * mm});
        }
        {
            var Q0;
            Q0=makeQuery(id+"F0.imprint","IMPRINT",FACE,{"disambiguationData":[TD([[makeQuery(id+"F0.imprint","IMPRINT",EDGE,{"derivedFrom":sQuery(id+"F0.wireOp",EDGE,"E91")}),1.0]])]});
            extrude(context, id + "F4", {"entities" : qUnion([Q0]), "operationType" : NewBodyOperationType.ADD, "depth" : -1.8 * mm, "offsetDistance" : 25 * mm});
        }
        {
            var Q0;
            Q0=makeQuery(id+"F0.imprint","IMPRINT",FACE,{"disambiguationData":[TD([[makeQuery(id+"F0.imprint","IMPRINT",EDGE,{"derivedFrom":sQuery(id+"F0.wireOp",EDGE,"E95")}),1.0]])]});
            extrude(context, id + "F5", {"entities" : qUnion([Q0]), "operationType" : NewBodyOperationType.ADD, "depth" : -1.8 * mm, "offsetDistance" : 25 * mm});
        }
        {
            var Q0;
            Q0=makeQuery(id+"F0.imprint","IMPRINT",FACE,{"disambiguationData":[TD([[makeQuery(id+"F0.imprint","IMPRINT",EDGE,{"derivedFrom":sQuery(id+"F0.wireOp",EDGE,"E92")}),1.0]])]});
            extrude(context, id + "F6", {"entities" : qUnion([Q0]), "operationType" : NewBodyOperationType.ADD, "depth" : -17 * mm, "offsetDistance" : 25 * mm});
        }
        {
            var Q0;
            Q0=makeQuery(id+"F0.imprint","IMPRINT",FACE,{"disambiguationData":[TD([[makeQuery(id+"F0.imprint","IMPRINT",EDGE,{"derivedFrom":sQuery(id+"F0.wireOp",EDGE,"E93")}),1.0]])]});
            extrude(context, id + "F7", {"entities" : qUnion([Q0]), "operationType" : NewBodyOperationType.ADD, "depth" : -1.8 * mm, "offsetDistance" : 25 * mm});
        }
        {
            var Q0;
            Q0=makeQuery(id+"F0.imprint","IMPRINT",FACE,{"disambiguationData":[TD([[makeQuery(id+"F0.imprint","IMPRINT",EDGE,{"derivedFrom":sQuery(id+"F0.wireOp",EDGE,"E96")}),1.0]])]});
            extrude(context, id + "F8", {"entities" : qUnion([Q0]), "operationType" : NewBodyOperationType.ADD, "depth" : -17 * mm, "offsetDistance" : 25 * mm});
        }
        {
            var Q0;
            Q0=makeQuery(id+"F0.imprint","IMPRINT",FACE,{"disambiguationData":[TD([[makeQuery(id+"F0.imprint","IMPRINT",EDGE,{"derivedFrom":sQuery(id+"F0.wireOp",EDGE,"E97")}),1.0]])]});
            extrude(context, id + "F9", {"entities" : qUnion([Q0]), "operationType" : NewBodyOperationType.ADD, "depth" : -1.8 * mm, "offsetDistance" : 25 * mm});
        }
        {
            var Q0;
            Q0=makeQuery(id+"F0.imprint","IMPRINT",FACE,{"disambiguationData":[TD([[makeQuery(id+"F0.imprint","IMPRINT",EDGE,{"derivedFrom":sQuery(id+"F0.wireOp",EDGE,"E94")}),1.0]])]});
            extrude(context, id + "F10", {"entities" : qUnion([Q0]), "operationType" : NewBodyOperationType.ADD, "depth" : -17 * mm, "offsetDistance" : 25 * mm});
        }
        {
            var Q0;
            Q0=makeQuery(id+"F1.opExtrude","SWEPT_FACE",FACE,{"disambiguationData":[OSD([sQuery(id+"F0.wireOp",EDGE,"E0.left")])]});
            var sketch = newSketch(context, id + "F11", { "sketchPlane" : qUnion([Q0])});
            skLineSegment(sketch, "E112", {"start": v(18, 50) * mm, "end": v(13.5, 50) * mm});
            skLineSegment(sketch, "E113", {"start": v(11, 47.5) * mm, "end": v(11, -47.5) * mm});
            skLineSegment(sketch, "E114", {"start": v(13.5, -50) * mm, "end": v(18, -50) * mm});
            skPoint(sketch, "E115.visualSharp", {"position": v(11, 50) * mm});
            skArc(sketch, "E115.filletArc", {"start": v(13.5, 50) * mm, "mid": v(11.73, 49.27) * mm, "end": v(11, 47.5) * mm});
            skPoint(sketch, "E116.visualSharp", {"position": v(11, -50) * mm});
            skArc(sketch, "E116.filletArc", {"start": v(11, -47.5) * mm, "mid": v(11.73, -49.27) * mm, "end": v(13.5, -50) * mm});
            skSolve(sketch);
        }
        {
            var Q0;
            {var subQ1=sQuery(id+"F11.wireOp",EDGE,"E112");Q0=makeQuery(id+"F11.imprint","IMPRINT",FACE,{"disambiguationData":[TD([[makeQuery(id+"F11.imprint","IMPRINT",EDGE,{"derivedFrom":subQ1}),1.0]])]});}
            extrude(context, id + "F12", {"entities" : qUnion([Q0]), "operationType" : NewBodyOperationType.REMOVE, "depth" : -325 * mm, "offsetDistance" : 25 * mm});
        }
        {
            var Q0;
            Q0=makeQuery(id+"F0.imprint","IMPRINT",FACE,{"disambiguationData":[TD([[makeQuery(id+"F0.imprint","IMPRINT",EDGE,{"derivedFrom":sQuery(id+"F0.wireOp",EDGE,"E98")}),1.0]])]});
            extrude(context, id + "F13", {"entities" : qUnion([Q0]), "operationType" : NewBodyOperationType.ADD, "depth" : -17 * mm, "offsetDistance" : 25 * mm});
        }
        {
            var Q0;
            Q0=makeQuery(id+"F0.imprint","IMPRINT",FACE,{"disambiguationData":[TD([[makeQuery(id+"F0.imprint","IMPRINT",EDGE,{"derivedFrom":sQuery(id+"F0.wireOp",EDGE,"E99")}),1.0]])]});
            extrude(context, id + "F14", {"entities" : qUnion([Q0]), "operationType" : NewBodyOperationType.ADD, "depth" : -1.8 * mm, "offsetDistance" : 25 * mm});
        }
        {
            var Q0;
            Q0=makeQuery(id+"F0.imprint","IMPRINT",FACE,{"disambiguationData":[TD([[makeQuery(id+"F0.imprint","IMPRINT",EDGE,{"derivedFrom":sQuery(id+"F0.wireOp",EDGE,"E102")}),1.0]])]});
            var Q1;
            Q1=makeQuery(id+"F0.imprint","IMPRINT",FACE,{"disambiguationData":[TD([[makeQuery(id+"F0.imprint","IMPRINT",EDGE,{"derivedFrom":sQuery(id+"F0.wireOp",EDGE,"E100")}),1.0]])]});
            extrude(context, id + "F15", {"entities" : qUnion([Q0, Q1]), "operationType" : NewBodyOperationType.ADD, "depth" : -17 * mm, "offsetDistance" : 25 * mm});
        }
        {
            var Q0;
            Q0=makeQuery(id+"F0.imprint","IMPRINT",FACE,{"disambiguationData":[TD([[makeQuery(id+"F0.imprint","IMPRINT",EDGE,{"derivedFrom":sQuery(id+"F0.wireOp",EDGE,"E103")}),1.0]])]});
            var Q1;
            Q1=makeQuery(id+"F0.imprint","IMPRINT",FACE,{"disambiguationData":[TD([[makeQuery(id+"F0.imprint","IMPRINT",EDGE,{"derivedFrom":sQuery(id+"F0.wireOp",EDGE,"E101")}),1.0]])]});
            extrude(context, id + "F16", {"entities" : qUnion([Q0, Q1]), "operationType" : NewBodyOperationType.ADD, "depth" : -1.8 * mm, "offsetDistance" : 25 * mm});
        }
        {
            var Q0;
            Q0=makeQuery(id+"F1.opExtrude","SWEPT_FACE",FACE,{"disambiguationData":[OSD([sQuery(id+"F0.wireOp",EDGE,"E87.left")])]});
            var sketch = newSketch(context, id + "F17", { "sketchPlane" : qUnion([Q0])});
            skLineSegment(sketch, "E117.bottom", {"start": v(-8.7, 32.2) * mm, "end": v(-7.2, 32.2) * mm});
            skLineSegment(sketch, "E117.top", {"start": v(-8.7, 20.4) * mm, "end": v(-7.2, 20.4) * mm});
            skLineSegment(sketch, "E117.left", {"start": v(-8.7, 32.2) * mm, "end": v(-8.7, 20.4) * mm});
            skLineSegment(sketch, "E117.right", {"start": v(-7.2, 32.2) * mm, "end": v(-7.2, 20.4) * mm});
            skLineSegment(sketch, "E118.bottom", {"start": v(-8.7, -20.4) * mm, "end": v(-7.2, -20.4) * mm});
            skLineSegment(sketch, "E118.top", {"start": v(-8.7, -32.2) * mm, "end": v(-7.2, -32.2) * mm});
            skLineSegment(sketch, "E118.left", {"start": v(-8.7, -20.4) * mm, "end": v(-8.7, -32.2) * mm});
            skLineSegment(sketch, "E118.right", {"start": v(-7.2, -20.4) * mm, "end": v(-7.2, -32.2) * mm});
            skSolve(sketch);
        }
        {
            var Q0;
            Q0=makeQuery(id+"F1.opExtrude","SWEPT_FACE",FACE,{"disambiguationData":[OSD([sQuery(id+"F0.wireOp",EDGE,"E87.right")])]});
            var sketch = newSketch(context, id + "F18", { "sketchPlane" : qUnion([Q0])});
            skLineSegment(sketch, "E119.bottom", {"start": v(8.12, 32.2) * mm, "end": v(9.62, 32.2) * mm});
            skLineSegment(sketch, "E119.top", {"start": v(8.12, 20.4) * mm, "end": v(9.62, 20.4) * mm});
            skLineSegment(sketch, "E119.left", {"start": v(8.12, 32.2) * mm, "end": v(8.12, 20.4) * mm});
            skLineSegment(sketch, "E119.right", {"start": v(9.62, 32.2) * mm, "end": v(9.62, 20.4) * mm});
            skLineSegment(sketch, "E120.bottom", {"start": v(8.12, -20.4) * mm, "end": v(9.62, -20.4) * mm});
            skLineSegment(sketch, "E120.top", {"start": v(8.12, -32.2) * mm, "end": v(9.62, -32.2) * mm});
            skLineSegment(sketch, "E120.left", {"start": v(8.12, -20.4) * mm, "end": v(8.12, -32.2) * mm});
            skLineSegment(sketch, "E120.right", {"start": v(9.62, -20.4) * mm, "end": v(9.62, -32.2) * mm});
            skSolve(sketch);
        }
        {
            var Q0;
            Q0=makeQuery(id+"F17.imprint","IMPRINT",FACE,{"disambiguationData":[TD([[makeQuery(id+"F17.imprint","IMPRINT",EDGE,{"derivedFrom":sQuery(id+"F17.wireOp",EDGE,"E117.bottom")}),-1.0]])]});
            var Q1;
            Q1=makeQuery(id+"F17.imprint","IMPRINT",FACE,{"disambiguationData":[TD([[makeQuery(id+"F17.imprint","IMPRINT",EDGE,{"derivedFrom":sQuery(id+"F17.wireOp",EDGE,"E118.bottom")}),-1.0]])]});
            var Q2;
            Q2=makeQuery(id+"F18.imprint","IMPRINT",FACE,{"disambiguationData":[TD([[makeQuery(id+"F18.imprint","IMPRINT",EDGE,{"derivedFrom":sQuery(id+"F18.wireOp",EDGE,"E119.bottom")}),-1.0]])]});
            var Q3;
            Q3=makeQuery(id+"F18.imprint","IMPRINT",FACE,{"disambiguationData":[TD([[makeQuery(id+"F18.imprint","IMPRINT",EDGE,{"derivedFrom":sQuery(id+"F18.wireOp",EDGE,"E120.bottom")}),-1.0]])]});
            extrude(context, id + "F19", {"entities" : qUnion([Q0, Q1, Q2, Q3]), "operationType" : NewBodyOperationType.ADD, "depth" : 1 * mm, "offsetDistance" : 25 * mm, "symmetric" : true});
        }
        {
            var Q0;
            Q0=makeQuery(id+"F19.opExtrude","CAP_FACE",FACE,{"disambiguationData":[OSD([sQuery(id+"F17.wireOp",EDGE,"E117.bottom"),sQuery(id+"F17.wireOp",EDGE,"E117.top"),sQuery(id+"F17.wireOp",EDGE,"E117.left"),sQuery(id+"F17.wireOp",EDGE,"E117.right")])],"isStart":false});
            var Q1;
            Q1=makeQuery(id+"F19.opExtrude","CAP_FACE",FACE,{"disambiguationData":[OSD([sQuery(id+"F17.wireOp",EDGE,"E118.bottom"),sQuery(id+"F17.wireOp",EDGE,"E118.top"),sQuery(id+"F17.wireOp",EDGE,"E118.left"),sQuery(id+"F17.wireOp",EDGE,"E118.right")])],"isStart":false});
            var Q2;
            Q2=makeQuery(id+"F19.opExtrude","SWEPT_EDGE",EDGE,{"disambiguationData":[OSD([sQuery(id+"F17.wireOp",EDGE,"E118.top"),sQuery(id+"F17.wireOp",EDGE,"E118.left")])]});
            var Q3;
            Q3=makeQuery(id+"F19.opExtrude","SWEPT_EDGE",EDGE,{"disambiguationData":[OSD([sQuery(id+"F17.wireOp",EDGE,"E118.top"),sQuery(id+"F17.wireOp",EDGE,"E118.right")])]});
            var Q4;
            Q4=makeQuery(id+"F19.opExtrude","SWEPT_EDGE",EDGE,{"disambiguationData":[OSD([sQuery(id+"F17.wireOp",EDGE,"E118.bottom"),sQuery(id+"F17.wireOp",EDGE,"E118.right")])]});
            var Q5;
            Q5=makeQuery(id+"F19.opExtrude","SWEPT_EDGE",EDGE,{"disambiguationData":[OSD([sQuery(id+"F17.wireOp",EDGE,"E118.bottom"),sQuery(id+"F17.wireOp",EDGE,"E118.left")])]});
            var Q6;
            Q6=makeQuery(id+"F19.opExtrude","SWEPT_EDGE",EDGE,{"disambiguationData":[OSD([sQuery(id+"F17.wireOp",EDGE,"E117.bottom"),sQuery(id+"F17.wireOp",EDGE,"E117.left")])]});
            var Q7;
            Q7=makeQuery(id+"F19.opExtrude","SWEPT_EDGE",EDGE,{"disambiguationData":[OSD([sQuery(id+"F17.wireOp",EDGE,"E117.bottom"),sQuery(id+"F17.wireOp",EDGE,"E117.right")])]});
            var Q8;
            Q8=makeQuery(id+"F19.opExtrude","SWEPT_EDGE",EDGE,{"disambiguationData":[OSD([sQuery(id+"F17.wireOp",EDGE,"E117.top"),sQuery(id+"F17.wireOp",EDGE,"E117.left")])]});
            var Q9;
            Q9=makeQuery(id+"F19.opExtrude","SWEPT_EDGE",EDGE,{"disambiguationData":[OSD([sQuery(id+"F17.wireOp",EDGE,"E117.top"),sQuery(id+"F17.wireOp",EDGE,"E117.right")])]});
            var Q10;
            Q10=makeQuery(id+"F19.opExtrude","CAP_FACE",FACE,{"disambiguationData":[OSD([sQuery(id+"F18.wireOp",EDGE,"E119.bottom"),sQuery(id+"F18.wireOp",EDGE,"E119.top"),sQuery(id+"F18.wireOp",EDGE,"E119.left"),sQuery(id+"F18.wireOp",EDGE,"E119.right")])],"isStart":true});
            var Q11;
            Q11=makeQuery(id+"F19.opExtrude","CAP_FACE",FACE,{"disambiguationData":[OSD([sQuery(id+"F18.wireOp",EDGE,"E120.bottom"),sQuery(id+"F18.wireOp",EDGE,"E120.top"),sQuery(id+"F18.wireOp",EDGE,"E120.left"),sQuery(id+"F18.wireOp",EDGE,"E120.right")])],"isStart":true});
            var Q12;
            Q12=makeQuery(id+"F19.opExtrude","SWEPT_EDGE",EDGE,{"disambiguationData":[OSD([sQuery(id+"F18.wireOp",EDGE,"E120.bottom"),sQuery(id+"F18.wireOp",EDGE,"E120.right")])]});
            var Q13;
            Q13=makeQuery(id+"F19.opExtrude","SWEPT_EDGE",EDGE,{"disambiguationData":[OSD([sQuery(id+"F18.wireOp",EDGE,"E120.top"),sQuery(id+"F18.wireOp",EDGE,"E120.right")])]});
            var Q14;
            Q14=makeQuery(id+"F19.opExtrude","SWEPT_EDGE",EDGE,{"disambiguationData":[OSD([sQuery(id+"F18.wireOp",EDGE,"E120.top"),sQuery(id+"F18.wireOp",EDGE,"E120.left")])]});
            var Q15;
            Q15=makeQuery(id+"F19.opExtrude","SWEPT_EDGE",EDGE,{"disambiguationData":[OSD([sQuery(id+"F18.wireOp",EDGE,"E120.bottom"),sQuery(id+"F18.wireOp",EDGE,"E120.left")])]});
            var Q16;
            Q16=makeQuery(id+"F19.opExtrude","SWEPT_EDGE",EDGE,{"disambiguationData":[OSD([sQuery(id+"F18.wireOp",EDGE,"E119.top"),sQuery(id+"F18.wireOp",EDGE,"E119.left")])]});
            var Q17;
            Q17=makeQuery(id+"F19.opExtrude","SWEPT_EDGE",EDGE,{"disambiguationData":[OSD([sQuery(id+"F18.wireOp",EDGE,"E119.top"),sQuery(id+"F18.wireOp",EDGE,"E119.right")])]});
            var Q18;
            Q18=makeQuery(id+"F19.opExtrude","SWEPT_EDGE",EDGE,{"disambiguationData":[OSD([sQuery(id+"F18.wireOp",EDGE,"E119.bottom"),sQuery(id+"F18.wireOp",EDGE,"E119.right")])]});
            var Q19;
            Q19=makeQuery(id+"F19.opExtrude","SWEPT_EDGE",EDGE,{"disambiguationData":[OSD([sQuery(id+"F18.wireOp",EDGE,"E119.bottom"),sQuery(id+"F18.wireOp",EDGE,"E119.left")])]});
            fillet(context, id + "F20", {"entities" : qUnion([Q0, Q1, Q2, Q3, Q4, Q5, Q6, Q7, Q8, Q9, Q10, Q11, Q12, Q13, Q14, Q15, Q16, Q17, Q18, Q19]), "radius" : 0.5 * mm, "tangentPropagation" : true, "allowEdgeOverflow" : false});
        }
    });
